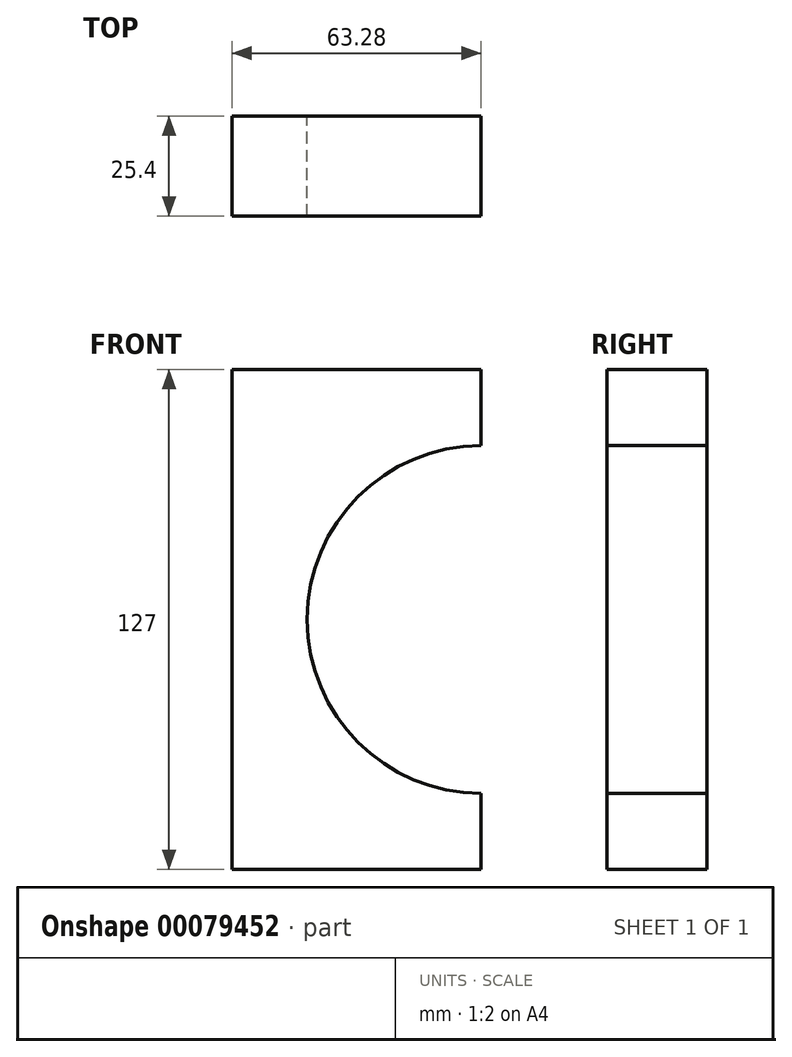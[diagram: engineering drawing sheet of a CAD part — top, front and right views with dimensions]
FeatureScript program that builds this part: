
annotation { "Feature Type Name" : "Feature", "Feature Type Description" : "" }
export const myFeature = defineFeature(function(context is Context, id is Id, definition is map)
    precondition{}
    {
        {
            var Q0;
            Q0=qCreatedBy(makeId("Front.planeOp"),FACE);
            var sketch = newSketch(context, id + "F0", { "sketchPlane" : qUnion([Q0])});
            skLineSegment(sketch, "E0.bottom", {"start": v(-46.46, 76.63) * mm, "end": v(16.82, 76.63) * mm});
            skLineSegment(sketch, "E0.top", {"start": v(-46.46, -50.37) * mm, "end": v(16.82, -50.37) * mm});
            skLineSegment(sketch, "E0.left", {"start": v(-46.46, 76.63) * mm, "end": v(-46.46, -50.37) * mm});
            skLineSegment(sketch, "E0.right", {"start": v(16.82, 76.63) * mm, "end": v(16.82, 57.3) * mm});
            skArc(sketch, "E1", {"start": v(16.82, 57.3) * mm, "mid": v(-27.36, 13.13) * mm, "end": v(16.82, -31.05) * mm});
            skPoint(sketch, "E2.start.orphan", {"position": v(-46.46, 13.13) * mm});
            skLineSegment(sketch, "E3.trimOffspring", {"start": v(16.82, -31.05) * mm, "end": v(16.82, -50.37) * mm});
            skSolve(sketch);
        }
        {
            var Q0;
            Q0=qSketchRegion(id+"F0",true);
            extrude(context, id + "F1", {"entities" : qUnion([Q0]), "depth" : 25.4 * mm});
        }
    });
